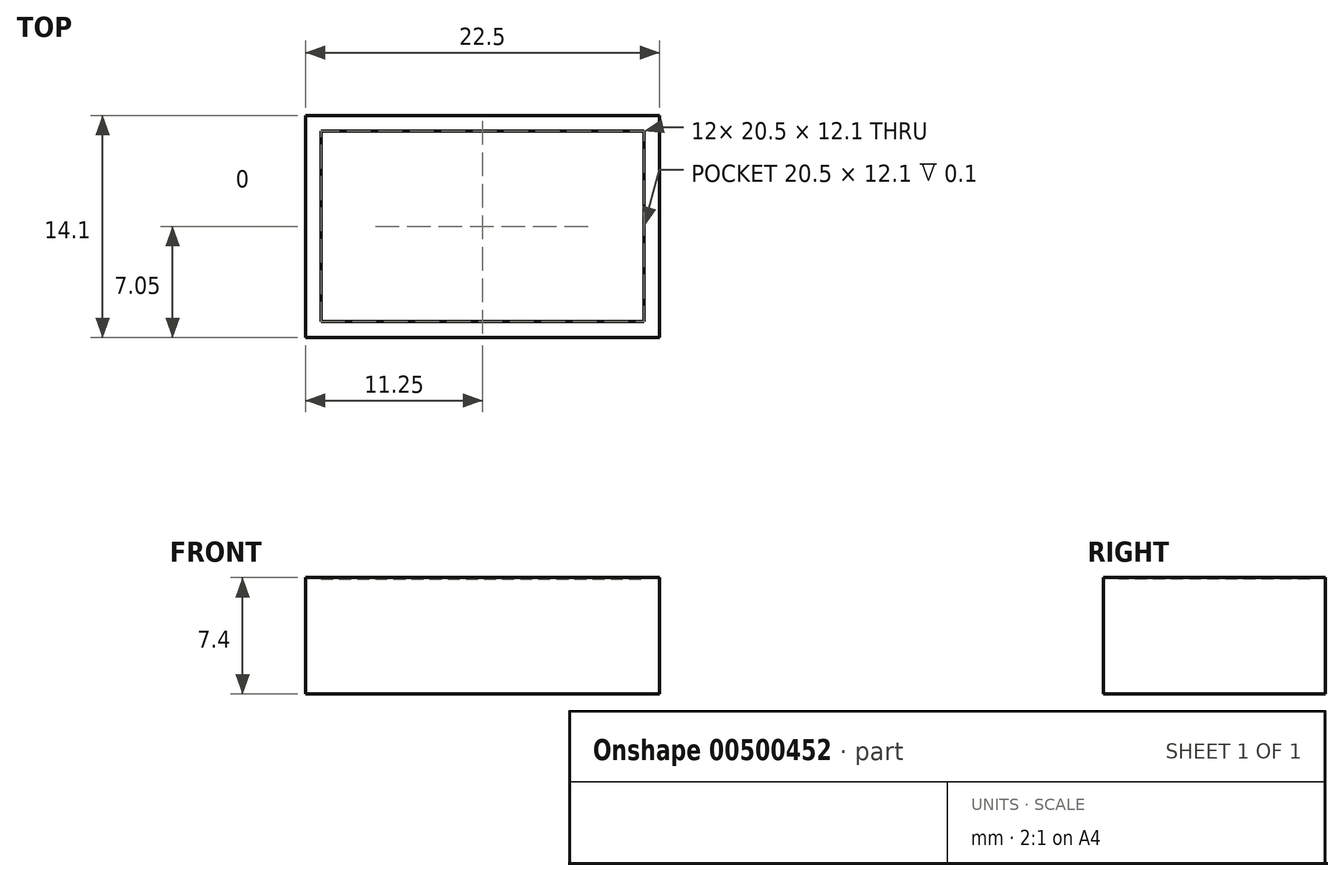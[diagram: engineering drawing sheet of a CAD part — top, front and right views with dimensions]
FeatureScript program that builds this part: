
annotation { "Feature Type Name" : "Feature", "Feature Type Description" : "" }
export const myFeature = defineFeature(function(context is Context, id is Id, definition is map)
    precondition{}
    {
        {
            var Q0;
            Q0=qCreatedBy(makeId("Top.planeOp"),FACE);
            var sketch = newSketch(context, id + "F0", { "sketchPlane" : qUnion([Q0])});
            skLineSegment(sketch, "E0.bottom", {"start": v(11.25, 7.05) * mm, "end": v(-11.25, 7.05) * mm});
            skLineSegment(sketch, "E0.top", {"start": v(11.25, -7.05) * mm, "end": v(-11.25, -7.05) * mm});
            skLineSegment(sketch, "E0.left", {"start": v(11.25, 7.05) * mm, "end": v(11.25, -7.05) * mm});
            skLineSegment(sketch, "E0.right", {"start": v(-11.25, 7.05) * mm, "end": v(-11.25, -7.05) * mm});
            skPoint(sketch, "E0.middle", {"position": v(0, 0) * mm});
            skSolve(sketch);
        }
        {
            var Q0;
            Q0 = qSketchRegion(id + "F0", true);
            extrude(context, id + "F1", {"entities" : qUnion([Q0]), "depth" : 7.4 * mm});
        }
        {
            var Q0;
            Q0=makeQuery(id+"F1.opExtrude","CAP_FACE",FACE,{"disambiguationData":[OSD([sQuery(id+"F0.wireOp",EDGE,"E0.bottom"),sQuery(id+"F0.wireOp",EDGE,"E0.top"),sQuery(id+"F0.wireOp",EDGE,"E0.left"),sQuery(id+"F0.wireOp",EDGE,"E0.right")])],"isStart":false});
            var sketch = newSketch(context, id + "F2", { "sketchPlane" : qUnion([Q0])});
            skLineSegment(sketch, "E1.0", {"start": v(-10.25, -6.05) * mm, "end": v(10.25, -6.05) * mm});
            skLineSegment(sketch, "E1.1", {"start": v(-10.25, 6.05) * mm, "end": v(-10.25, -6.05) * mm});
            skLineSegment(sketch, "E1.2", {"start": v(10.25, 6.05) * mm, "end": v(-10.25, 6.05) * mm});
            skLineSegment(sketch, "E1.3", {"start": v(10.25, -6.05) * mm, "end": v(10.25, 6.05) * mm});
            skSolve(sketch);
        }
        {
            var Q0;
            Q0 = qSketchRegion(id + "F2", true);
            extrude(context, id + "F3", {"entities" : qUnion([Q0]), "operationType" : NewBodyOperationType.REMOVE, "oppositeDirection" : true, "depth" : .1 * mm, "offsetDistance" : 25 * mm});
        }
    });
